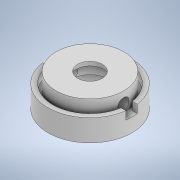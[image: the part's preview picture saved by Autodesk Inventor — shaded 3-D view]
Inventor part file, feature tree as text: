
AUTODESK INVENTOR PART (.ipt)
format: ipt  version: 2022 (Build 260153000, 153)  size: 205,312 bytes
history: native  units: mm
features: sketch x4, extrude x3, plane x2, revolve x1
ambient origin geometry x8: Origin, YZ Plane, XZ Plane, XY Plane, X Axis, Y Axis, Z Axis, Center Point
bodies: Solid1 (feature_tree)
feature tree (10):
  revolve  "Revolution1"  [1 undecoded]
  extrude  "Extrusion1"  Depth=3.0mm
  plane  "Work Plane1"
  extrude  "Extrusion2"  Depth=7.0mm
  plane  "Work Plane2"
  extrude  "Extrusion3"  Depth=10.0mm
  sketch  "Sketch2"  dims[d3=20.875mm d4=11.5mm]
  sketch  "Sketch3"  dims[d5=2.0mm d6=3.0mm]
  sketch  "Sketch4"  dims[d7=6.5mm d9=7.0mm]
  sketch  "Sketch5"  dims[d10=14.1mm d11=3.0mm d12=7.6mm d13=10.0mm d15=360.0deg d16=7.05mm d17=0.0mm d20=7.0mm d21=0.0mm d22=0.0mm d23=-28.0mm d24=7.0mm d25=10.0mm d26=0.0mm d27=28.0mm d28=7.0mm d29=10.0mm d30=0.0mm d31=2.5mm d33=10.0mm]
note: 1 required parameter value undecoded (feature->parameter linkage not recoverable at this tier; creation-order binding heuristic only, values carry confidence <= 0.55)
